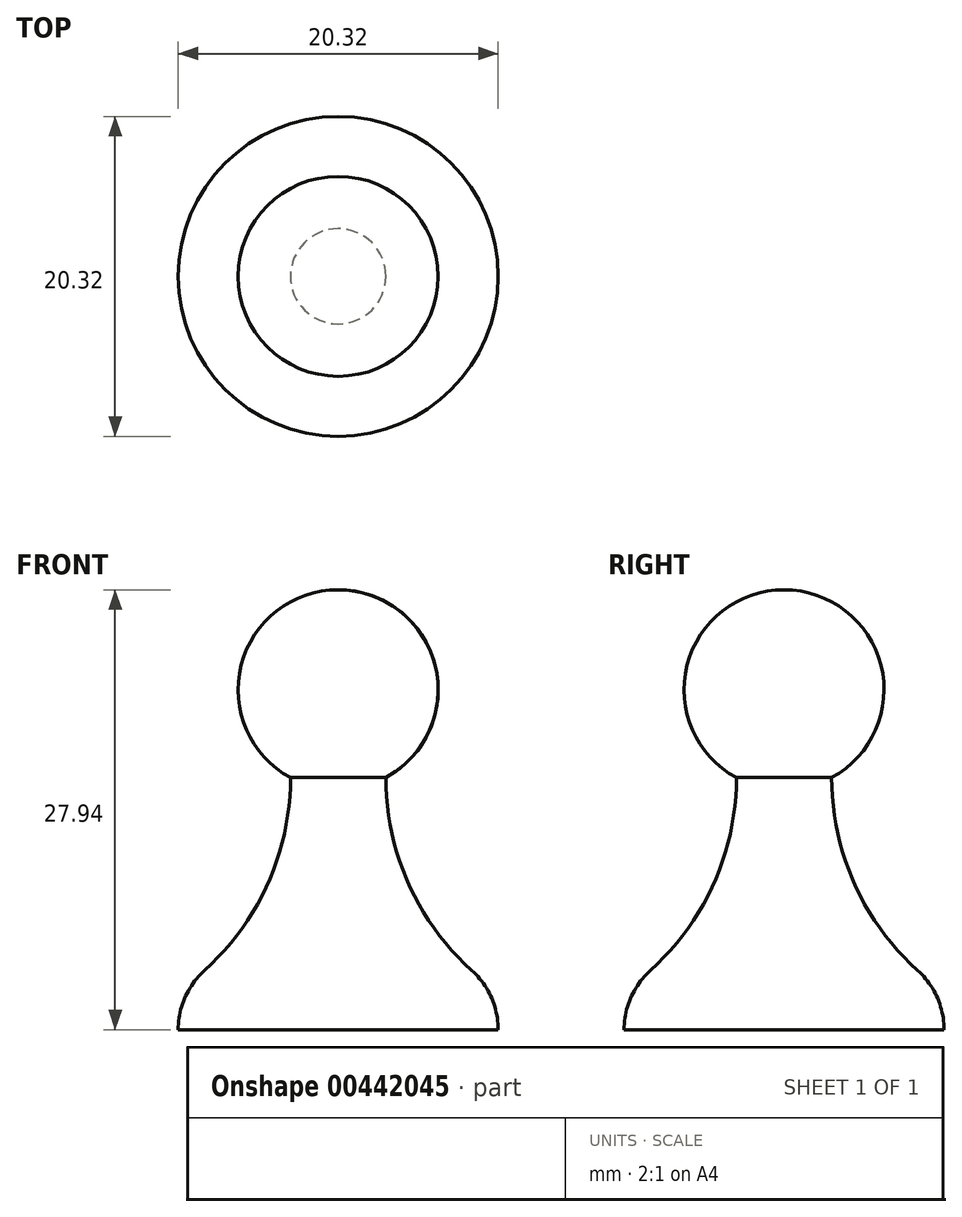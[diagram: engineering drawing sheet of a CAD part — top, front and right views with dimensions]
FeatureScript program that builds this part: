
annotation { "Feature Type Name" : "Feature", "Feature Type Description" : "" }
export const myFeature = defineFeature(function(context is Context, id is Id, definition is map)
    precondition{}
    {
        {
            var Q0;
            Q0=qCreatedBy(makeId("Front.planeOp"),FACE);
            var sketch = newSketch(context, id + "F0", { "sketchPlane" : qUnion([Q0])});
            skArc(sketch, "E0", {"start": v(0, 27.94) * mm, "mid": v(-6.35, 21.6) * mm, "end": v(0, 15.24) * mm});
            skLineSegment(sketch, "E1", {"start": v(0, 0) * mm, "end": v(-10.16, 0) * mm});
            skArc(sketch, "E2", {"start": v(-8.48, 3.77) * mm, "mid": v(-9.72, 2.07) * mm, "end": v(-10.16, 0) * mm});
            skArc(sketch, "E3", {"start": v(-8.48, 3.77) * mm, "mid": v(-4.45, 9.31) * mm, "end": v(-3.02, 16) * mm});
            skLineSegment(sketch, "E4", {"start": v(-3.02, 16) * mm, "end": v(-3.02, 0) * mm, "construction": true});
            skLineSegment(sketch, "E5", {"start": v(0, 27.94) * mm, "end": v(0, 0) * mm});
            skLineSegment(sketch, "E6", {"start": v(-10.16, 0) * mm, "end": v(-10.16, 3.2) * mm, "construction": true});
            skSolve(sketch);
        }
        {
            var Q0;
            Q0=qSketchRegion(id+"F0",true);
            var Q1;
            Q1=sQuery(id+"F0.wireOp",EDGE,"E5");
            revolve(context, id + "F1", {"entities" : qUnion([Q0]), "axis" : qUnion([Q1]), "revolveType" : RevolveType.FULL});
        }
    });
